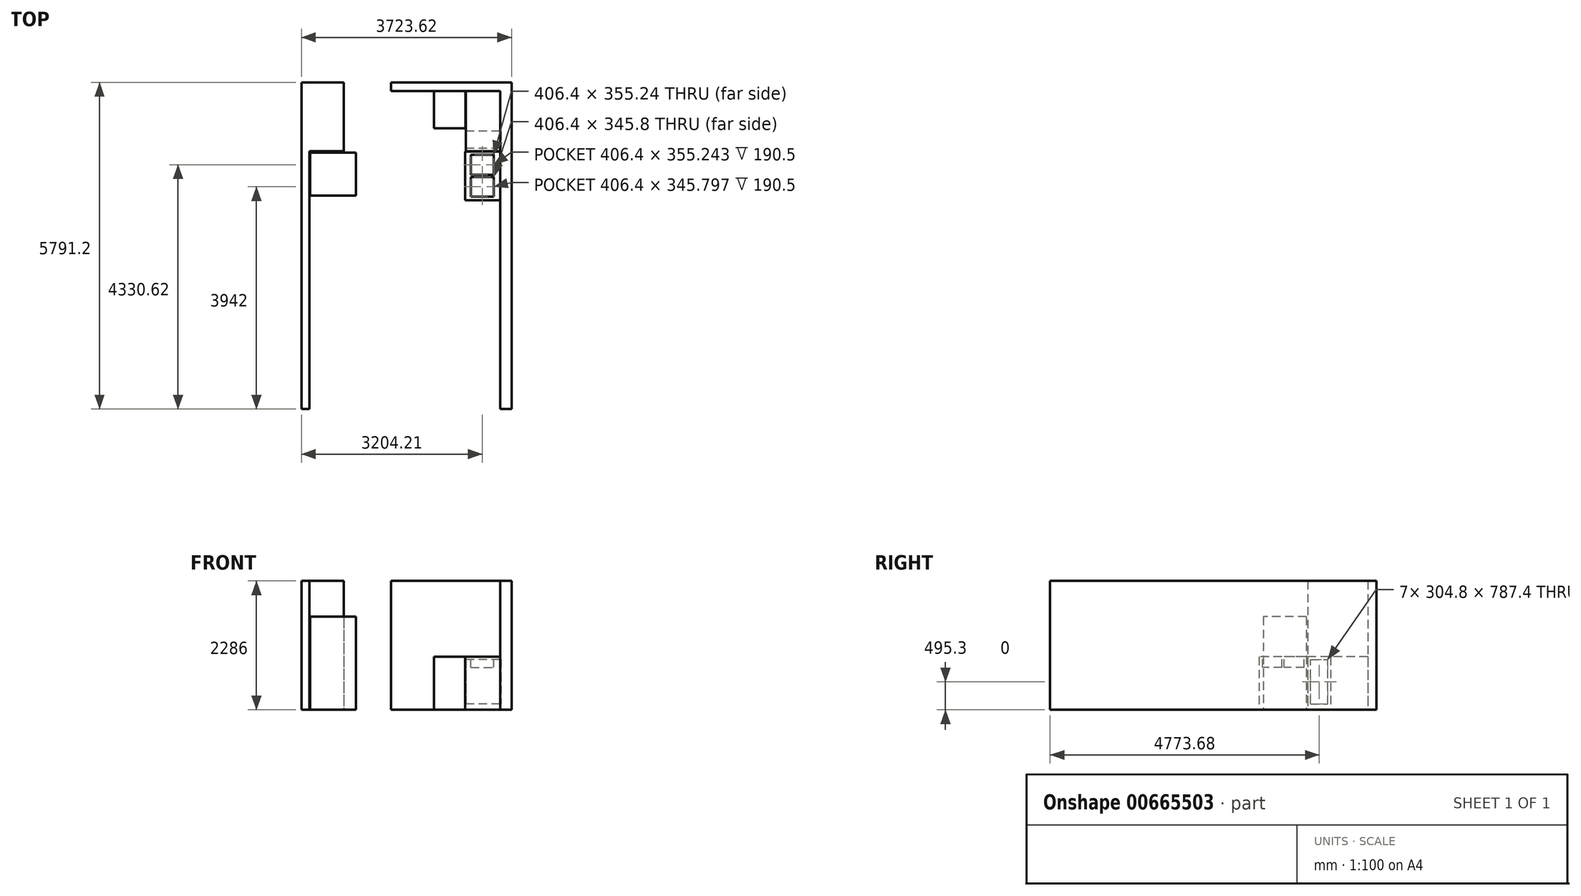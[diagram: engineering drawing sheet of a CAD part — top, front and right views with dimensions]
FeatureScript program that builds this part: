
annotation { "Feature Type Name" : "Feature", "Feature Type Description" : "" }
export const myFeature = defineFeature(function(context is Context, id is Id, definition is map)
    precondition{}
    {
        {
            var Q0;
            Q0=qCreatedBy(makeId("Top.planeOp"),FACE);
            var sketch = newSketch(context, id + "F0", { "sketchPlane" : qUnion([Q0])});
            skLineSegment(sketch, "E0.bottom", {"start": v(-695.51, -3810) * mm, "end": v(-555.81, -3810) * mm});
            skLineSegment(sketch, "E0.top", {"start": v(-695.51, 762) * mm, "end": v(-555.81, 762) * mm});
            skLineSegment(sketch, "E0.left", {"start": v(-695.51, -3810) * mm, "end": v(-695.51, 762) * mm});
            skLineSegment(sketch, "E0.right", {"start": v(-555.81, -3810) * mm, "end": v(-555.81, 762) * mm});
            skLineSegment(sketch, "E1.top", {"start": v(-790.66, 1064.24) * mm, "end": v(-788.44, 1064.24) * mm});
            skPoint(sketch, "E2.top.end.orphan", {"position": v(283.38, 3766.22) * mm});
            skPoint(sketch, "E3.orphan", {"position": v(283.38, 1956.84) * mm});
            skPoint(sketch, "E4.orphan", {"position": v(-98.35, 1064.24) * mm});
            skPoint(sketch, "E5.bottom.start.orphan", {"position": v(593.97, 1064.24) * mm});
            skLineSegment(sketch, "E6.bottom", {"start": v(-695.51, 762) * mm, "end": v(53.79, 762) * mm});
            skLineSegment(sketch, "E6.top", {"start": v(-695.51, 1981.2) * mm, "end": v(53.79, 1981.2) * mm});
            skLineSegment(sketch, "E6.left", {"start": v(-695.51, 762) * mm, "end": v(-695.51, 1981.2) * mm});
            skLineSegment(sketch, "E6.right", {"start": v(53.79, 762) * mm, "end": v(53.79, 1981.2) * mm});
            skLineSegment(sketch, "E7.bottom", {"start": v(891.99, 1981.2) * mm, "end": v(2828.74, 1981.2) * mm});
            skLineSegment(sketch, "E7.top", {"start": v(891.99, 1828.8) * mm, "end": v(2828.74, 1828.8) * mm});
            skLineSegment(sketch, "E7.left", {"start": v(891.99, 1981.2) * mm, "end": v(891.99, 1828.8) * mm});
            skLineSegment(sketch, "E7.right", {"start": v(2828.74, 1981.2) * mm, "end": v(2828.74, 1828.8) * mm});
            skLineSegment(sketch, "E8.bottom", {"start": v(2828.74, 1981.2) * mm, "end": v(3028.11, 1981.2) * mm});
            skLineSegment(sketch, "E8.top", {"start": v(2828.74, -3810) * mm, "end": v(3028.11, -3810) * mm});
            skLineSegment(sketch, "E8.left", {"start": v(2828.74, 1981.2) * mm, "end": v(2828.74, -3810) * mm});
            skLineSegment(sketch, "E8.right", {"start": v(3028.11, 1981.2) * mm, "end": v(3028.11, -3810) * mm});
            skLineSegment(sketch, "E9.bottom", {"start": v(891.99, 1828.8) * mm, "end": v(1095.19, 1828.8) * mm});
            skLineSegment(sketch, "E10", {"start": v(-695.51, 1981.2) * mm, "end": v(3028.11, 1981.2) * mm});
            skLineSegment(sketch, "E11.bottom", {"start": v(-555.81, 762) * mm, "end": v(53.79, 762) * mm});
            skLineSegment(sketch, "E11.left", {"start": v(-555.81, 762) * mm, "end": v(-555.81, 0) * mm});
            skPoint(sketch, "E11.top.end.orphan", {"position": v(245.5, 0) * mm});
            skPoint(sketch, "E12.right.end.orphan", {"position": v(2174.69, 1289.05) * mm});
            skPoint(sketch, "E13.top.end.orphan", {"position": v(2181.04, 368.3) * mm});
            skPoint(sketch, "E14.left.start.orphan", {"position": v(2181.04, 361.95) * mm});
            skSolve(sketch);
        }
        {
            var Q0;
            {var subQ1=sQuery(id+"F0.wireOp",EDGE,"E7.top");Q0=makeQuery(id+"F0.imprint","IMPRINT",FACE,{"disambiguationData":[TD([[makeQuery(id+"F0.imprint","IMPRINT",EDGE,{"derivedFrom":subQ1}),1.0]])]});}
            var Q1;
            {var subQ3=sQuery(id+"F0.wireOp",EDGE,"E8.top");Q1=makeQuery(id+"F0.imprint","IMPRINT",FACE,{"disambiguationData":[TD([[makeQuery(id+"F0.imprint","IMPRINT",EDGE,{"derivedFrom":subQ3}),1.0]])]});}
            var Q2;
            Q2=makeQuery(id+"F0.imprint","IMPRINT",FACE,{"disambiguationData":[TD([[makeQuery(id+"F0.imprint","IMPRINT",EDGE,{"derivedFrom":sQuery(id+"F0.wireOp",EDGE,"E0.bottom")}),1.0]])]});
            var Q3;
            Q3=makeQuery(id+"F0.imprint","IMPRINT",FACE,{"disambiguationData":[TD([[makeQuery(id+"F0.imprint","IMPRINT",EDGE,{"derivedFrom":sQuery(id+"F0.wireOp",EDGE,"E6.bottom")}),1.0]])]});
            extrude(context, id + "F1", {"entities" : qUnion([Q0, Q1, Q2, Q3]), "depth" : 2286 * mm, "offsetDistance" : 25.4 * mm});
        }
        {
            var Q0;
            Q0=qCreatedBy(makeId("Top.planeOp"),FACE);
            var sketch = newSketch(context, id + "F2", { "sketchPlane" : qUnion([Q0])});
            skLineSegment(sketch, "E15.bottom", {"start": v(-543.11, 736.6) * mm, "end": v(269.69, 736.6) * mm});
            skLineSegment(sketch, "E15.top", {"start": v(-543.11, -25.4) * mm, "end": v(269.69, -25.4) * mm});
            skLineSegment(sketch, "E15.left", {"start": v(-543.11, 736.6) * mm, "end": v(-543.11, -25.4) * mm});
            skLineSegment(sketch, "E15.right", {"start": v(269.69, 736.6) * mm, "end": v(269.69, -25.4) * mm});
            skSolve(sketch);
        }
        {
            var Q0;
            Q0 = qSketchRegion(id + "F2", true);
            extrude(context, id + "F3", {"entities" : qUnion([Q0]), "depth" : 1651 * mm, "offsetDistance" : 25.4 * mm});
        }
        {
            var Q0;
            Q0=qCreatedBy(makeId("Top.planeOp"),FACE);
            var sketch = newSketch(context, id + "F4", { "sketchPlane" : qUnion([Q0])});
            skLineSegment(sketch, "E16.bottom", {"start": v(2826.2, 1828.55) * mm, "end": v(2216.6, 1828.55) * mm});
            skLineSegment(sketch, "E16.top", {"start": v(2826.2, 761.75) * mm, "end": v(2216.6, 761.75) * mm});
            skLineSegment(sketch, "E16.left", {"start": v(2826.2, 1828.55) * mm, "end": v(2826.2, 761.75) * mm});
            skLineSegment(sketch, "E16.right", {"start": v(2216.6, 1828.55) * mm, "end": v(2216.6, 761.75) * mm});
            skLineSegment(sketch, "E17.bottom", {"start": v(1655.26, 1826.26) * mm, "end": v(2214.06, 1826.26) * mm});
            skLineSegment(sketch, "E17.top", {"start": v(1655.26, 1165.86) * mm, "end": v(2214.06, 1165.86) * mm});
            skLineSegment(sketch, "E17.left", {"start": v(1655.26, 1826.26) * mm, "end": v(1655.26, 1165.86) * mm});
            skLineSegment(sketch, "E17.right", {"start": v(2214.06, 1826.26) * mm, "end": v(2214.06, 1165.86) * mm});
            skSolve(sketch);
        }
        {
            var Q0;
            Q0 = qSketchRegion(id + "F4", true);
            extrude(context, id + "F5", {"entities" : qUnion([Q0]), "depth" : 939.8 * mm, "offsetDistance" : 25.4 * mm});
        }
        {
            var Q0;
            Q0 = qSketchRegion(id + "F4", true);
            extrude(context, id + "F6", {"entities" : qUnion([Q0]), "depth" : 939.8 * mm, "offsetDistance" : 25.4 * mm});
        }
        {
            var Q0;
            Q0=makeQuery(id+"F5.opExtrude","SWEPT_FACE",FACE,{"disambiguationData":[OSD([sQuery(id+"F4.wireOp",EDGE,"E16.right")])]});
            var sketch = newSketch(context, id + "F7", { "sketchPlane" : qUnion([Q0])});
            skLineSegment(sketch, "E18.bottom", {"start": v(-1116.08, 889) * mm, "end": v(-811.28, 889) * mm});
            skLineSegment(sketch, "E18.top", {"start": v(-1116.08, 101.6) * mm, "end": v(-811.28, 101.6) * mm});
            skLineSegment(sketch, "E18.left", {"start": v(-1116.08, 889) * mm, "end": v(-1116.08, 101.6) * mm});
            skLineSegment(sketch, "E18.right", {"start": v(-811.28, 889) * mm, "end": v(-811.28, 101.6) * mm});
            skSolve(sketch);
        }
        {
            var Q0;
            Q0=makeQuery(id+"F7.imprint","IMPRINT",FACE,{"disambiguationData":[TD([[makeQuery(id+"F7.imprint","IMPRINT",EDGE,{"derivedFrom":sQuery(id+"F7.wireOp",EDGE,"E18.bottom")}),-1.0]])]});
            extrude(context, id + "F8", {"entities" : qUnion([Q0]), "operationType" : NewBodyOperationType.REMOVE, "oppositeDirection" : true, "depth" : 622.3 * mm, "offsetDistance" : 25.4 * mm});
        }
        {
            var Q0;
            Q0=qCreatedBy(makeId("Top.planeOp"),FACE);
            var sketch = newSketch(context, id + "F9", { "sketchPlane" : qUnion([Q0])});
            skLineSegment(sketch, "E19.bottom", {"start": v(2203.9, 759.2) * mm, "end": v(2826.2, 759.2) * mm});
            skLineSegment(sketch, "E19.top", {"start": v(2203.9, -104.4) * mm, "end": v(2826.2, -104.4) * mm});
            skLineSegment(sketch, "E19.left", {"start": v(2203.9, 759.2) * mm, "end": v(2203.9, -104.4) * mm});
            skLineSegment(sketch, "E19.right", {"start": v(2826.2, 759.2) * mm, "end": v(2826.2, -104.4) * mm});
            skSolve(sketch);
        }
        {
            var Q0;
            Q0 = qSketchRegion(id + "F9", true);
            extrude(context, id + "F10", {"entities" : qUnion([Q0]), "depth" : 939.8 * mm, "offsetDistance" : 25.4 * mm});
        }
        {
            var Q0;
            Q0=makeQuery(id+"F10.opExtrude","CAP_FACE",FACE,{"disambiguationData":[OSD([sQuery(id+"F9.wireOp",EDGE,"E19.bottom"),sQuery(id+"F9.wireOp",EDGE,"E19.top"),sQuery(id+"F9.wireOp",EDGE,"E19.left"),sQuery(id+"F9.wireOp",EDGE,"E19.right")])],"isStart":false});
            var sketch = newSketch(context, id + "F11", { "sketchPlane" : qUnion([Q0])});
            skLineSegment(sketch, "E20.bottom", {"start": v(2305.5, 698.25) * mm, "end": v(2711.9, 698.25) * mm});
            skLineSegment(sketch, "E20.top", {"start": v(2305.5, 343) * mm, "end": v(2711.9, 343) * mm});
            skLineSegment(sketch, "E20.left", {"start": v(2305.5, 698.25) * mm, "end": v(2305.5, 343) * mm});
            skLineSegment(sketch, "E20.right", {"start": v(2711.9, 698.25) * mm, "end": v(2711.9, 343) * mm});
            skLineSegment(sketch, "E21.bottom", {"start": v(2305.5, 304.9) * mm, "end": v(2711.9, 304.9) * mm});
            skLineSegment(sketch, "E21.top", {"start": v(2305.5, -40.9) * mm, "end": v(2711.9, -40.9) * mm});
            skLineSegment(sketch, "E21.left", {"start": v(2305.5, 304.9) * mm, "end": v(2305.5, -40.9) * mm});
            skLineSegment(sketch, "E21.right", {"start": v(2711.9, 304.9) * mm, "end": v(2711.9, -40.9) * mm});
            skSolve(sketch);
        }
        {
            var Q0;
            Q0=makeQuery(id+"F11.imprint","IMPRINT",FACE,{"disambiguationData":[TD([[makeQuery(id+"F11.imprint","IMPRINT",EDGE,{"derivedFrom":sQuery(id+"F11.wireOp",EDGE,"E21.bottom")}),-1.0]])]});
            var Q1;
            Q1=makeQuery(id+"F11.imprint","IMPRINT",FACE,{"disambiguationData":[TD([[makeQuery(id+"F11.imprint","IMPRINT",EDGE,{"derivedFrom":sQuery(id+"F11.wireOp",EDGE,"E20.bottom")}),-1.0]])]});
            extrude(context, id + "F12", {"entities" : qUnion([Q0, Q1]), "operationType" : NewBodyOperationType.REMOVE, "oppositeDirection" : true, "depth" : 190.5 * mm, "offsetDistance" : 25.4 * mm});
        }
    });
